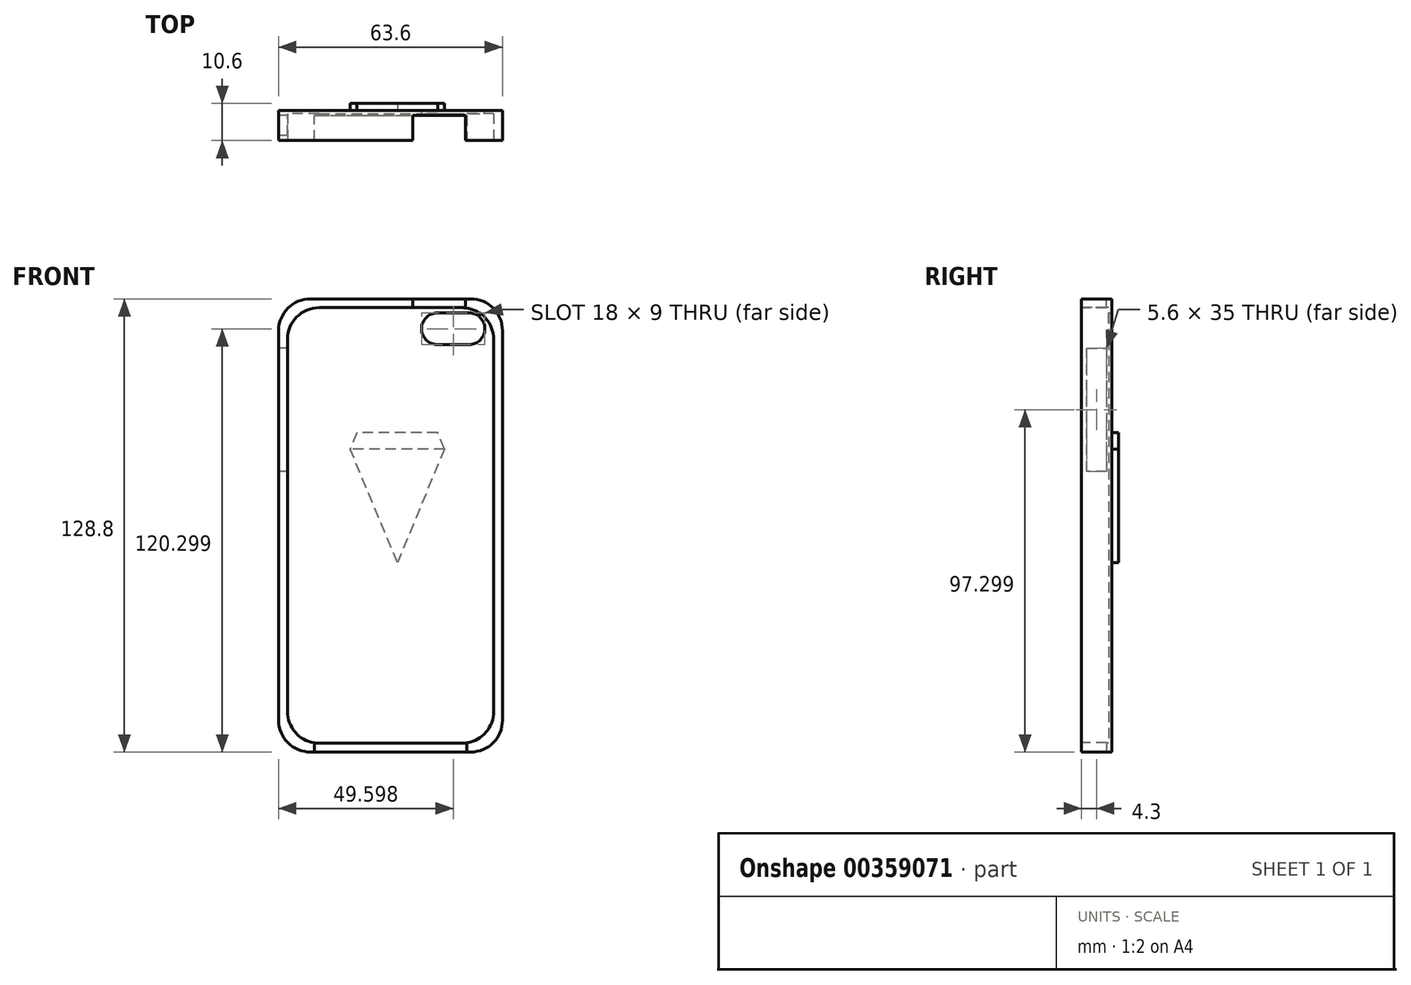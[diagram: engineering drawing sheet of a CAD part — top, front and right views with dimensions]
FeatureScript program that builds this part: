
annotation { "Feature Type Name" : "Feature", "Feature Type Description" : "" }
export const myFeature = defineFeature(function(context is Context, id is Id, definition is map)
    precondition{}
    {
        {
            var Q0;
            Q0=qCreatedBy(makeId("Front.planeOp"),FACE);
            var sketch = newSketch(context, id + "F0", { "sketchPlane" : qUnion([Q0])});
            skLineSegment(sketch, "E0.bottom", {"start": v(-11.34, 74.98) * mm, "end": v(34.26, 74.98) * mm});
            skLineSegment(sketch, "E0.top", {"start": v(-11.34, -53.82) * mm, "end": v(34.26, -53.82) * mm});
            skLineSegment(sketch, "E0.left", {"start": v(-20.34, 65.98) * mm, "end": v(-20.34, -44.82) * mm});
            skLineSegment(sketch, "E0.right", {"start": v(43.26, 65.98) * mm, "end": v(43.26, -44.82) * mm});
            skPoint(sketch, "E1.visualSharp", {"position": v(-20.34, 74.98) * mm});
            skArc(sketch, "E1.filletArc", {"start": v(-11.34, 74.98) * mm, "mid": v(-17.7, 72.34) * mm, "end": v(-20.34, 65.98) * mm});
            skPoint(sketch, "E2.visualSharp", {"position": v(-20.34, -53.82) * mm});
            skArc(sketch, "E2.filletArc", {"start": v(-20.34, -44.82) * mm, "mid": v(-17.7, -51.18) * mm, "end": v(-11.34, -53.82) * mm});
            skPoint(sketch, "E3.visualSharp", {"position": v(43.26, -53.82) * mm});
            skArc(sketch, "E3.filletArc", {"start": v(34.26, -53.82) * mm, "mid": v(40.62, -51.18) * mm, "end": v(43.26, -44.82) * mm});
            skPoint(sketch, "E4.visualSharp", {"position": v(43.26, 74.98) * mm});
            skArc(sketch, "E4.filletArc", {"start": v(43.26, 65.98) * mm, "mid": v(40.62, 72.34) * mm, "end": v(34.26, 74.98) * mm});
            skSolve(sketch);
        }
        {
            var Q0;
            Q0 = qSketchRegion(id + "F0", true);
            extrude(context, id + "F1", {"entities" : qUnion([Q0]), "depth" : 8.6 * mm});
        }
        {
            var Q0;
            Q0=makeQuery(id+"F1.opExtrude","CAP_FACE",FACE,{"disambiguationData":[OSD([sQuery(id+"F0.wireOp",EDGE,"E0.bottom"),sQuery(id+"F0.wireOp",EDGE,"E0.top"),sQuery(id+"F0.wireOp",EDGE,"E0.left"),sQuery(id+"F0.wireOp",EDGE,"E0.right"),sQuery(id+"F0.wireOp",EDGE,"E1.filletArc"),sQuery(id+"F0.wireOp",EDGE,"E2.filletArc"),sQuery(id+"F0.wireOp",EDGE,"E3.filletArc"),sQuery(id+"F0.wireOp",EDGE,"E4.filletArc")])],"isStart":false});
            var sketch = newSketch(context, id + "F2", { "sketchPlane" : qUnion([Q0])});
            skLineSegment(sketch, "E5.bottom", {"start": v(-8.84, 72.48) * mm, "end": v(31.76, 72.48) * mm});
            skLineSegment(sketch, "E5.top", {"start": v(-8.84, -51.32) * mm, "end": v(31.76, -51.32) * mm});
            skLineSegment(sketch, "E5.left", {"start": v(-17.84, 63.48) * mm, "end": v(-17.84, -42.32) * mm});
            skLineSegment(sketch, "E5.right", {"start": v(40.76, 63.48) * mm, "end": v(40.76, -42.32) * mm});
            skPoint(sketch, "E6.visualSharp", {"position": v(-17.84, 72.48) * mm});
            skArc(sketch, "E6.filletArc", {"start": v(-8.84, 72.48) * mm, "mid": v(-15.2, 69.84) * mm, "end": v(-17.84, 63.48) * mm});
            skPoint(sketch, "E7.visualSharp", {"position": v(40.76, 72.48) * mm});
            skArc(sketch, "E7.filletArc", {"start": v(40.76, 63.48) * mm, "mid": v(38.12, 69.84) * mm, "end": v(31.76, 72.48) * mm});
            skPoint(sketch, "E8.visualSharp", {"position": v(40.76, -51.32) * mm});
            skArc(sketch, "E8.filletArc", {"start": v(31.76, -51.32) * mm, "mid": v(38.12, -48.68) * mm, "end": v(40.76, -42.32) * mm});
            skPoint(sketch, "E9.visualSharp", {"position": v(-17.84, -51.32) * mm});
            skArc(sketch, "E9.filletArc", {"start": v(-17.84, -42.32) * mm, "mid": v(-15.2, -48.68) * mm, "end": v(-8.84, -51.32) * mm});
            skSolve(sketch);
        }
        {
            var Q0;
            Q0 = qSketchRegion(id + "F2", true);
            extrude(context, id + "F3", {"entities" : qUnion([Q0]), "operationType" : NewBodyOperationType.REMOVE, "oppositeDirection" : true, "depth" : 7.7 * mm});
        }
        {
            var Q0;
            Q0=makeQuery(id+"F1.opExtrude","CAP_FACE",FACE,{"disambiguationData":[OSD([sQuery(id+"F0.wireOp",EDGE,"E0.bottom"),sQuery(id+"F0.wireOp",EDGE,"E0.top"),sQuery(id+"F0.wireOp",EDGE,"E0.left"),sQuery(id+"F0.wireOp",EDGE,"E0.right"),sQuery(id+"F0.wireOp",EDGE,"E1.filletArc"),sQuery(id+"F0.wireOp",EDGE,"E2.filletArc"),sQuery(id+"F0.wireOp",EDGE,"E3.filletArc"),sQuery(id+"F0.wireOp",EDGE,"E4.filletArc")])],"isStart":true});
            var sketch = newSketch(context, id + "F4", { "sketchPlane" : qUnion([Q0])});
            skLineSegment(sketch, "E10.bottom", {"start": v(-33.76, 70.98) * mm, "end": v(-24.76, 70.98) * mm});
            skLineSegment(sketch, "E10.top", {"start": v(-33.76, 61.98) * mm, "end": v(-24.76, 61.98) * mm});
            skLineSegment(sketch, "E10.left", {"start": v(-38.26, 66.48) * mm, "end": v(-38.26, 66.48) * mm});
            skLineSegment(sketch, "E10.right", {"start": v(-20.26, 66.48) * mm, "end": v(-20.26, 66.48) * mm});
            skPoint(sketch, "E11.visualSharp", {"position": v(-38.26, 70.98) * mm});
            skArc(sketch, "E11.filletArc", {"start": v(-33.76, 70.98) * mm, "mid": v(-36.94, 69.66) * mm, "end": v(-38.26, 66.48) * mm});
            skPoint(sketch, "E12.visualSharp", {"position": v(-38.26, 61.98) * mm});
            skArc(sketch, "E12.filletArc", {"start": v(-38.26, 66.48) * mm, "mid": v(-36.94, 63.3) * mm, "end": v(-33.76, 61.98) * mm});
            skPoint(sketch, "E13.visualSharp", {"position": v(-20.26, 61.98) * mm});
            skArc(sketch, "E13.filletArc", {"start": v(-24.76, 61.98) * mm, "mid": v(-21.58, 63.3) * mm, "end": v(-20.26, 66.48) * mm});
            skPoint(sketch, "E14.visualSharp", {"position": v(-20.26, 70.98) * mm});
            skArc(sketch, "E14.filletArc", {"start": v(-20.26, 66.48) * mm, "mid": v(-21.58, 69.66) * mm, "end": v(-24.76, 70.98) * mm});
            skSolve(sketch);
        }
        {
            var Q0;
            Q0 = qSketchRegion(id + "F4", true);
            extrude(context, id + "F5", {"entities" : qUnion([Q0]), "operationType" : NewBodyOperationType.REMOVE, "oppositeDirection" : true, "depth" : 5 * mm});
        }
        {
            var Q0;
            Q0=makeQuery(id+"F1.opExtrude","CAP_FACE",FACE,{"disambiguationData":[OSD([sQuery(id+"F0.wireOp",EDGE,"E0.bottom"),sQuery(id+"F0.wireOp",EDGE,"E0.top"),sQuery(id+"F0.wireOp",EDGE,"E0.left"),sQuery(id+"F0.wireOp",EDGE,"E0.right"),sQuery(id+"F0.wireOp",EDGE,"E1.filletArc"),sQuery(id+"F0.wireOp",EDGE,"E2.filletArc"),sQuery(id+"F0.wireOp",EDGE,"E3.filletArc"),sQuery(id+"F0.wireOp",EDGE,"E4.filletArc")])],"isStart":true});
            var sketch = newSketch(context, id + "F6", { "sketchPlane" : qUnion([Q0])});
            skLineSegment(sketch, "E15", {"start": v(-26.79, 32.34) * mm, "end": v(-13.4, 0) * mm});
            skLineSegment(sketch, "E16", {"start": v(-13.4, 0) * mm, "end": v(0, 32.34) * mm});
            skLineSegment(sketch, "E17", {"start": v(-26.79, 32.34) * mm, "end": v(-24.87, 36.96) * mm});
            skLineSegment(sketch, "E18", {"start": v(-24.87, 36.96) * mm, "end": v(-1.91, 36.96) * mm});
            skLineSegment(sketch, "E19", {"start": v(-1.91, 36.96) * mm, "end": v(0, 32.34) * mm});
            skSolve(sketch);
        }
        {
            var Q0;
            Q0 = qSketchRegion(id + "F6", true);
            extrude(context, id + "F7", {"entities" : qUnion([Q0]), "operationType" : NewBodyOperationType.ADD, "depth" : 1 * mm});
        }
        {
            var Q0;
            Q0=makeQuery(id+"F1.opExtrude","SWEPT_FACE",FACE,{"disambiguationData":[OSD([sQuery(id+"F0.wireOp",EDGE,"E0.top")])]});
            var sketch = newSketch(context, id + "F8", { "sketchPlane" : qUnion([Q0])});
            skLineSegment(sketch, "E20", {"start": v(-10.24, 8.6) * mm, "end": v(-10.24, 1.43) * mm});
            skLineSegment(sketch, "E21", {"start": v(-10.24, 1.43) * mm, "end": v(33.16, 1.43) * mm});
            skLineSegment(sketch, "E22", {"start": v(33.16, 1.43) * mm, "end": v(33.16, 8.6) * mm});
            skLineSegment(sketch, "E23", {"start": v(33.16, 8.6) * mm, "end": v(-10.24, 8.6) * mm});
            skSolve(sketch);
        }
        {
            var Q0;
            Q0 = qSketchRegion(id + "F8", true);
            extrude(context, id + "F9", {"entities" : qUnion([Q0]), "operationType" : NewBodyOperationType.REMOVE, "oppositeDirection" : true, "depth" : 25 * mm});
        }
        {
            var Q0;
            Q0=makeQuery(id+"F1.opExtrude","SWEPT_FACE",FACE,{"disambiguationData":[OSD([sQuery(id+"F0.wireOp",EDGE,"E0.bottom")])]});
            var sketch = newSketch(context, id + "F10", { "sketchPlane" : qUnion([Q0])});
            skLineSegment(sketch, "E24", {"start": v(17.76, -8.6) * mm, "end": v(17.76, -1.5) * mm});
            skLineSegment(sketch, "E25", {"start": v(17.76, -1.5) * mm, "end": v(32.76, -1.5) * mm});
            skLineSegment(sketch, "E26", {"start": v(32.76, -1.5) * mm, "end": v(32.76, -8.6) * mm});
            skLineSegment(sketch, "E27", {"start": v(17.76, -8.6) * mm, "end": v(32.76, -8.6) * mm});
            skSolve(sketch);
        }
        {
            var Q0;
            Q0 = qSketchRegion(id + "F10", true);
            extrude(context, id + "F11", {"entities" : qUnion([Q0]), "operationType" : NewBodyOperationType.REMOVE, "oppositeDirection" : true, "depth" : 25 * mm});
        }
        {
            var Q0;
            Q0=makeQuery(id+"F1.opExtrude","SWEPT_FACE",FACE,{"disambiguationData":[OSD([sQuery(id+"F0.wireOp",EDGE,"E0.left")])]});
            var sketch = newSketch(context, id + "F12", { "sketchPlane" : qUnion([Q0])});
            skLineSegment(sketch, "E28", {"start": v(1.5, 60.98) * mm, "end": v(1.5, 25.98) * mm});
            skLineSegment(sketch, "E29", {"start": v(1.5, 25.98) * mm, "end": v(7.1, 25.98) * mm});
            skLineSegment(sketch, "E30", {"start": v(7.1, 25.98) * mm, "end": v(7.1, 60.98) * mm});
            skLineSegment(sketch, "E31", {"start": v(7.1, 60.98) * mm, "end": v(1.5, 60.98) * mm});
            skSolve(sketch);
        }
        {
            var Q0;
            Q0 = qSketchRegion(id + "F12", true);
            var Q1;
            Q1 = qSketchRegion(id + "F14", true);
            extrude(context, id + "F13", {"entities" : qUnion([Q0, Q1]), "operationType" : NewBodyOperationType.REMOVE, "oppositeDirection" : true, "depth" : 25 * mm});
        }
        {
            var Q0;
            Q0=makeQuery(id+"F7.opExtrude","CAP_FACE",FACE,{"disambiguationData":[OSD([sQuery(id+"F6.wireOp",EDGE,"E15"),sQuery(id+"F6.wireOp",EDGE,"E16"),sQuery(id+"F6.wireOp",EDGE,"E17"),sQuery(id+"F6.wireOp",EDGE,"E18"),sQuery(id+"F6.wireOp",EDGE,"E19")])],"isStart":false});
            var sketch = newSketch(context, id + "F14", { "sketchPlane" : qUnion([Q0])});
            skLineSegment(sketch, "E32", {"start": v(-26.79, 32.34) * mm, "end": v(0, 32.34) * mm});
            skSolve(sketch);
        }
        {
            var Q0;
            Q0=makeQuery(id+"F14.imprint","IMPRINT",FACE,{"disambiguationData":[TD([[makeQuery(id+"F14.imprint","IMPRINT",EDGE,{"derivedFrom":sQuery(id+"F14.wireOp",EDGE,"E32")}),1.0]])]});
            extrude(context, id + "F15", {"entities" : qUnion([Q0]), "operationType" : NewBodyOperationType.ADD, "depth" : 1 * mm});
        }
        {
            var Q0;
            Q0=makeQuery(id+"F7.opExtrude","CAP_FACE",FACE,{"disambiguationData":[OSD([sQuery(id+"F6.wireOp",EDGE,"E15"),sQuery(id+"F6.wireOp",EDGE,"E16"),sQuery(id+"F6.wireOp",EDGE,"E17"),sQuery(id+"F6.wireOp",EDGE,"E18"),sQuery(id+"F6.wireOp",EDGE,"E19")])],"isStart":false});
            var sketch = newSketch(context, id + "F16", { "sketchPlane" : qUnion([Q0])});
            skLineSegment(sketch, "E33", {"start": v(-26.79, 32.34) * mm, "end": v(-13.4, 0) * mm});
            skLineSegment(sketch, "E34", {"start": v(-13.4, 0) * mm, "end": v(0, 32.34) * mm});
            skLineSegment(sketch, "E35", {"start": v(0, 32.34) * mm, "end": v(-26.79, 32.34) * mm});
            skSolve(sketch);
        }
        {
            var Q0;
            Q0 = qSketchRegion(id + "F16", true);
            extrude(context, id + "F17", {"entities" : qUnion([Q0]), "operationType" : NewBodyOperationType.ADD, "depth" : 0.95 * mm});
        }
    });
